# Revit family: 203_FLEXIT-ABC-IRIS
name_source: partatom
category: Duct Accessories
revit_build: Autodesk Revit 2018 (Build: 20170223_1515(x64)
units: mm (PartAtom-declared; Revit-internal decimal feet)

## family parameters
Always vertical = Yes
Cut with Voids When Loaded = No
Part Type = Damper
Round Connector Dimension = Use Diameter
Shared = No
Work Plane-Based = No

## types (2) — shared parameters
CAT0 = Yes
Description = Iris damper
H2D = 100 mm  [stored 0.328084 ft]
L2D = 55 mm
Manufacturer = Flexit
QmdConnectorList = 201;D;202;D
URL = www.flexit.no
W2D = 100 mm  [stored 0.328084 ft]
magiPartTypeId = 203
magiProductFamilyId = FLEXIT-ABC-IRIS

## per-type parameters (varying)
| type | BD | D | L1 | L2 | LL | R | magiProductId |
| 100-115710 | 165 mm  [stored 0.541339 ft] | 100 mm | 14 mm  [stored 0.0459318 ft] | 21 mm | 28 mm | 50 mm  [stored 0.164042 ft] | FLEXIT-ABC-IRIS-100 |
| 125-115711 | 190 mm  [stored 0.62336 ft] | 125 mm | 15 mm  [stored 0.0492126 ft] | 23 mm | 30 mm  [stored 0.0984252 ft] | 63 mm | FLEXIT-ABC-IRIS-125 |

note: column(s) folded — value = type name in every type: MC Product Code

note: [stored X ft] marks values corroborated as IEEE doubles in the binary element streams (Revit-internal decimal feet)

## geometry (parser evidence)
native form markers: Sweep x2
no freeform markers — native parametric forms only
